# Revit family: VENTS-VKH_EC
name_source: partatom
category: Mechanical Equipment
units: mm (PartAtom-declared; Revit-internal decimal feet)

## family parameters
Always vertical = Yes
Classification = None
Cut with Voids When Loaded = No
OmniClass Number = 23.75.35.17.14
OmniClass Title = Fans, Single Units
Part Type = Normal
Room Calculation Point = No
Round Connector Dimension = Use Diameter
Shared = No
Work Plane-Based = No

## types (11) — shared parameters
Casing Material = Fan Zinc
Description = Centrifugal roof fan with horizontal air discharge
Family Version = 1.0
Grid Material = Grid Cross Zinc
Hb = 30 mm  [stored 0.0984252 ft]
Ht2 = 22 mm  [stored 0.0721785 ft]
Load Classification = HVAC
Maintenance Zone Front Depth = 400 mm  [stored 1.31234 ft]
Maintenance Zone Material = Maintenance Zone
Maintenance Zone Side Depth = 400 mm  [stored 1.31234 ft]
Manufacturer = Vents
Power Factor = 1
Protection rating = IP X4
URL = https://ventilation-system.com
grGap1 = 1 mm  [stored 0.00328084 ft]
grGap2 = 20 mm  [stored 0.0656168 ft]
zero-valued in all types: Sound Pressure Level at 1 m (dBA), Sound Pressure Level at 3 m (dBA)

## per-type parameters (varying)
| type | A | Ac | Atop | Current | D | Duct Connection Size | H | Hc | Ht1 | L | Maximum Air Flow | Noise Level at 3 m (dBa) | Number of Poles | RPM (min-1) | Transported Air Temperature (°C) | Type Comments | Voltage | Weight | gsA |
| VKH 190 EC | 351 mm  [stored 1.15157 ft] | 298 mm  [stored 0.97769 ft] | 294 mm  [stored 0.964567 ft] | 1 A | 213 mm  [stored 0.698819 ft] | 180 mm  [stored 0.590551 ft] | 189 mm  [stored 0.620079 ft] | 78 mm | 59 mm | 350 mm  [stored 1.14829 ft] | 670 m³/h | 52 | 1 | 3520 | -25...+60 | Centrifugal roof fan VKH 190 EC | 230 V | 8.00 kg | 281 mm |
| VKH 225 EC | 351 mm  [stored 1.15157 ft] | 298 mm  [stored 0.97769 ft] | 295 mm  [stored 0.967848 ft] | 1 A | 213 mm  [stored 0.698819 ft] | 180 mm  [stored 0.590551 ft] | 234 mm  [stored 0.767717 ft] | 123 mm  [stored 0.403543 ft] | 59 mm | 350 mm  [stored 1.14829 ft] | 1290 m³/h | 47 | 1 | 2400 | -25...+60 | Centrifugal roof fan VKH 225 EC | 230 V | 8.00 kg | 281 mm |
| VKH 250 EC | 451 mm | 398 mm  [stored 1.30577 ft] | 394 mm | 1 A | 285 mm  [stored 0.935039 ft] | 250 mm  [stored 0.82021 ft] | 237 mm  [stored 0.777559 ft] | 126 mm  [stored 0.413386 ft] | 59 mm | 450 mm | 1470 m³/h | 54 | 1 | 3300 | -25...+60 | Centrifugal roof fan VKH 250 EC | 230 V | 13.00 kg | 361 mm |
| VKH 280 EC | 451 mm | 398 mm  [stored 1.30577 ft] | 394 mm | 1 A | 285 mm  [stored 0.935039 ft] | 250 mm  [stored 0.82021 ft] | 263 mm  [stored 0.862861 ft] | 152 mm | 59 mm | 450 mm | 2330 m³/h | 48 | 1 | 2610 | -20...+60 | Centrifugal roof fan VKH 280 EC | 230 V | 13.00 kg | 361 mm |
| VKH 310 EC | 451 mm | 398 mm  [stored 1.30577 ft] | 394 mm | 2 A | 285 mm  [stored 0.935039 ft] | 250 mm  [stored 0.82021 ft] | 263 mm  [stored 0.862861 ft] | 152 mm | 59 mm | 450 mm | 3100 m³/h | 49 | 1 | 2600 | -20...+60 | Centrifugal roof fan VKH 310 EC | 230 V | 16.00 kg | 361 mm |
| VKH 355 EC | 625 mm | 568 mm | 534 mm | 9 A | 438 mm  [stored 1.43701 ft] | 400 mm  [stored 1.31234 ft] | 322 mm  [stored 1.05643 ft] | 176 mm  [stored 0.577428 ft] | 94 mm  [stored 0.308399 ft] | 620 mm | 3830 m³/h | 51 | 1 | 1550 | -25...+50 | Centrifugal roof fan VKH 355 EC | 230 V | 27.00 kg | 500 mm |
| VKH 400 EC | 625 mm | 568 mm | 534 mm | 4 A | 438 mm  [stored 1.43701 ft] | 400 mm  [stored 1.31234 ft] | 384 mm  [stored 1.25984 ft] | 238 mm | 94 mm  [stored 0.308399 ft] | 620 mm | 5380 m³/h | 58 | 1 | 1450 | -25...+50 | Centrifugal roof fan VKH 400 EC | 230 V | 27.00 kg | 500 mm |
| VKH 450 EC | 710 mm | 624 mm | 600 mm | 3 A | 438 mm  [stored 1.43701 ft] | 400 mm  [stored 1.31234 ft] | 420 mm  [stored 1.37795 ft] | 254 mm  [stored 0.833333 ft] | 114 mm  [stored 0.374016 ft] | 700 mm | 8110 m³/h | 63 | 3 | 1560 | -20...+60 | Centrifugal roof fan VKH 450 EC | 400 V | 46.00 kg | 568 mm |
| VKH 500 EC | 710 mm | 624 mm | 600 mm | 2 A | 445 mm  [stored 1.45997 ft] | 400 mm  [stored 1.31234 ft] | 467 mm | 301 mm  [stored 0.987533 ft] | 114 mm  [stored 0.374016 ft] | 700 mm | 10900 m³/h | 67 | 3 | 1480 | -25...+50 | Centrifugal roof fan VKH 500 EC | 400 V | 51.00 kg | 568 mm |
| VKH 560 EC | 900 mm | 838 mm | 790 mm | 4 A | 605 mm | 560 mm | 489 mm | 323 mm  [stored 1.05971 ft] | 114 mm  [stored 0.374016 ft] | 895 mm | 13640 m³/h | 69 | 3 | 1540 | -25...+60 | Centrifugal roof fan VKH 560 EC | 400 V | 71.00 kg | 720 mm |
| VKH 630 EC | 1000 mm | 915 mm | 892 mm | 5 A | 600 mm | 560 mm | 520 mm | 354 mm  [stored 1.16142 ft] | 114 mm  [stored 0.374016 ft] | 990 mm | 18270 m³/h | 71 | 3 | 1450 | -25...+55 | Centrifugal roof fan VKH 630 EC | 400 V | 101.00 kg | 800 mm |

note: column(s) folded — value = type name in every type: Model

note: [stored X ft] marks values corroborated as IEEE doubles in the binary element streams (Revit-internal decimal feet)

## geometry (parser evidence)
native form markers: Sweep x4
no freeform markers — native parametric forms only
